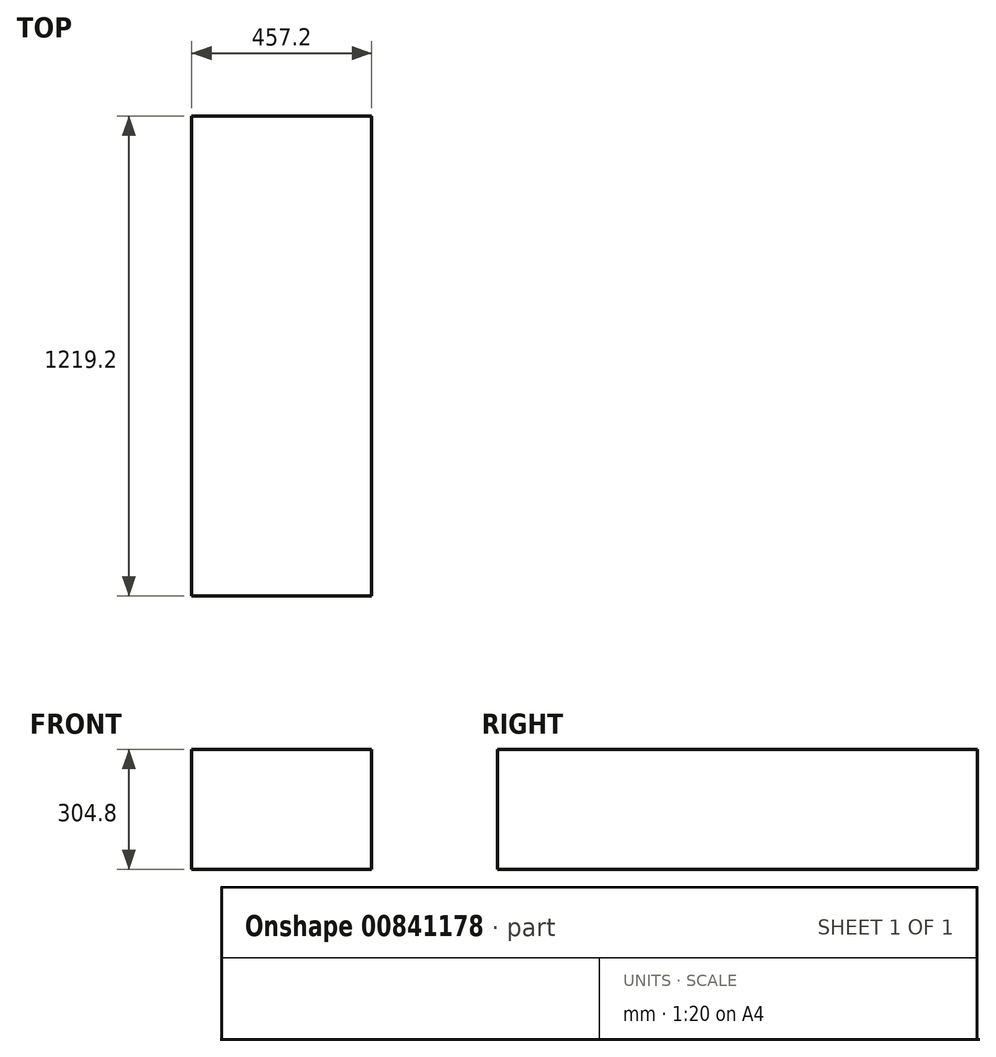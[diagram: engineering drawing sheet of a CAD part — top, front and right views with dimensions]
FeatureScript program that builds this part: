
annotation { "Feature Type Name" : "Feature", "Feature Type Description" : "" }
export const myFeature = defineFeature(function(context is Context, id is Id, definition is map)
    precondition{}
    {
        {
            var Q0;
            Q0=qCreatedBy(makeId("Front.planeOp"),FACE);
            var sketch = newSketch(context, id + "F0", { "sketchPlane" : qUnion([Q0])});
            skLineSegment(sketch, "E0.bottom", {"start": v(0, 0) * mm, "end": v(457.2, 0) * mm});
            skLineSegment(sketch, "E0.top", {"start": v(0, 304.8) * mm, "end": v(457.2, 304.8) * mm});
            skLineSegment(sketch, "E0.left", {"start": v(0, 0) * mm, "end": v(0, 304.8) * mm});
            skLineSegment(sketch, "E0.right", {"start": v(457.2, 0) * mm, "end": v(457.2, 304.8) * mm});
            skSolve(sketch);
        }
        {
            var Q0;
            Q0=makeQuery(id+"F0.imprint","IMPRINT",FACE,{"disambiguationData":[TD([[makeQuery(id+"F0.imprint","IMPRINT",EDGE,{"derivedFrom":sQuery(id+"F0.wireOp",EDGE,"E0.bottom")}),1.0]])]});
            extrude(context, id + "F1", {"entities" : qUnion([Q0]), "depth" : 1219.2 * mm, "offsetDistance" : 25.4 * mm});
        }
    });
